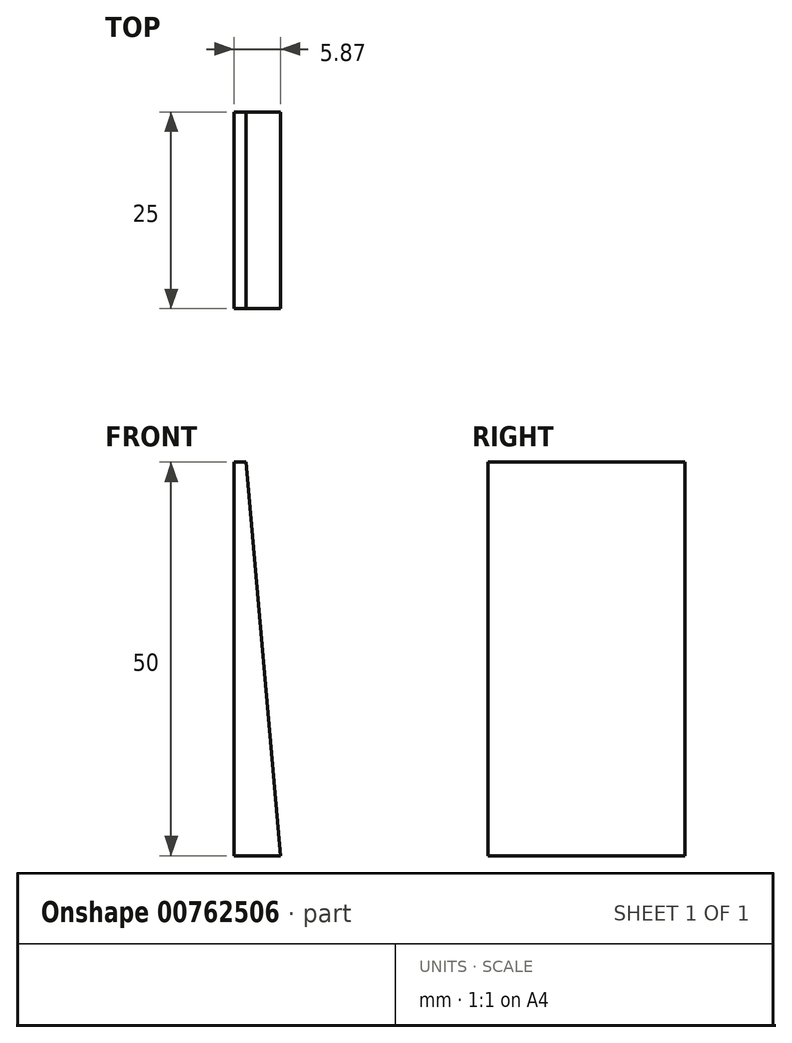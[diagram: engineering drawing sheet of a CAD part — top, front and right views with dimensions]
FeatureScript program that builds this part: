
annotation { "Feature Type Name" : "Feature", "Feature Type Description" : "" }
export const myFeature = defineFeature(function(context is Context, id is Id, definition is map)
    precondition{}
    {
        {
            var Q0;
            Q0=qCreatedBy(makeId("Front.planeOp"),FACE);
            var sketch = newSketch(context, id + "F0", { "sketchPlane" : qUnion([Q0])});
            skLineSegment(sketch, "E0", {"start": v(0, 0) * mm, "end": v(0, 50) * mm});
            skLineSegment(sketch, "E1", {"start": v(0, 50) * mm, "end": v(1.5, 50) * mm});
            skLineSegment(sketch, "E2", {"start": v(1.5, 50) * mm, "end": v(5.87, 0) * mm});
            skLineSegment(sketch, "E3", {"start": v(5.87, 0) * mm, "end": v(0, 0) * mm});
            skSolve(sketch);
        }
        {
            var Q0;
            Q0 = qSketchRegion(id + "F0", true);
            extrude(context, id + "F1", {"entities" : qUnion([Q0]), "oppositeDirection" : true, "depth" : 25 * mm, "offsetDistance" : 25 * mm});
        }
    });
